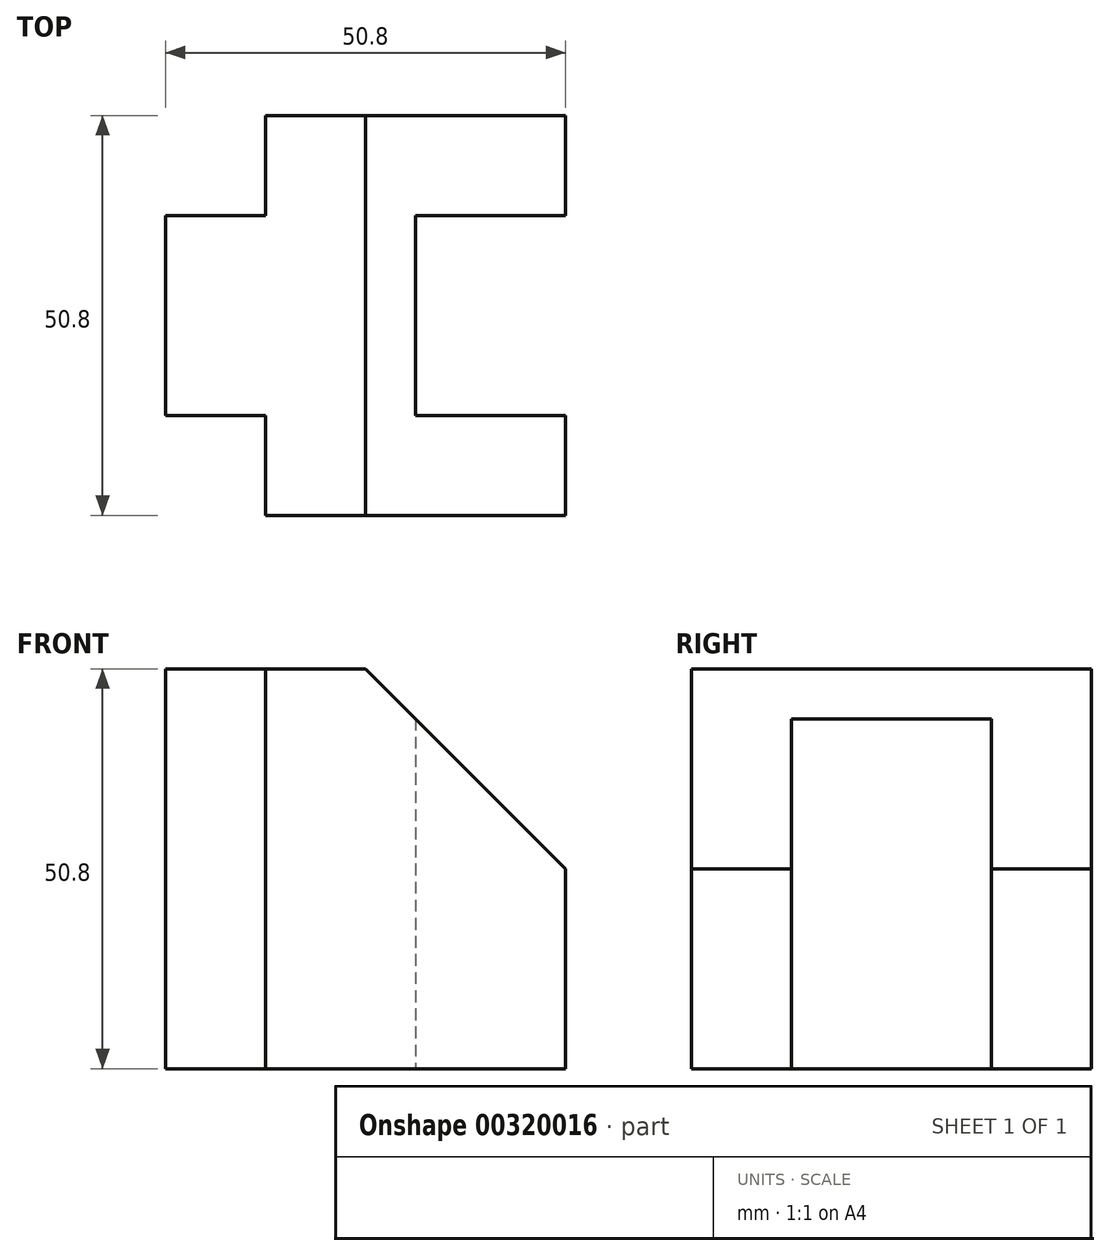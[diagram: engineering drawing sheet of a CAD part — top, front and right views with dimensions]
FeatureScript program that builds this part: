
annotation { "Feature Type Name" : "Feature", "Feature Type Description" : "" }
export const myFeature = defineFeature(function(context is Context, id is Id, definition is map)
    precondition{}
    {
        {
            var Q0;
            Q0=qCreatedBy(makeId("Top.planeOp"),FACE);
            var sketch = newSketch(context, id + "F0", { "sketchPlane" : qUnion([Q0])});
            skLineSegment(sketch, "E0", {"start": v(0, 12.7) * mm, "end": v(0, -12.7) * mm});
            skLineSegment(sketch, "E1", {"start": v(0, -12.7) * mm, "end": v(19.05, -12.7) * mm});
            skLineSegment(sketch, "E2", {"start": v(19.05, -12.7) * mm, "end": v(19.05, -25.4) * mm});
            skLineSegment(sketch, "E3", {"start": v(19.05, -25.4) * mm, "end": v(-19.05, -25.4) * mm});
            skLineSegment(sketch, "E4", {"start": v(-19.05, -25.4) * mm, "end": v(-19.05, -12.7) * mm});
            skLineSegment(sketch, "E5", {"start": v(-19.05, -12.7) * mm, "end": v(-31.75, -12.7) * mm});
            skLineSegment(sketch, "E6", {"start": v(-31.75, -12.7) * mm, "end": v(-31.75, 12.7) * mm});
            skLineSegment(sketch, "E7", {"start": v(-31.75, 12.7) * mm, "end": v(-19.05, 12.7) * mm});
            skLineSegment(sketch, "E8", {"start": v(-19.05, 12.7) * mm, "end": v(-19.05, 25.4) * mm});
            skLineSegment(sketch, "E9", {"start": v(-19.05, 25.4) * mm, "end": v(19.05, 25.4) * mm});
            skLineSegment(sketch, "E10", {"start": v(19.05, 25.4) * mm, "end": v(19.05, 12.7) * mm});
            skLineSegment(sketch, "E11", {"start": v(19.05, 12.7) * mm, "end": v(0, 12.7) * mm});
            skLineSegment(sketch, "E12", {"start": v(-6.35, 25.4) * mm, "end": v(-6.35, -25.4) * mm});
            skSolve(sketch);
        }
        {
            var Q0;
            {var subQ0=sQuery(id+"F0.wireOp",EDGE,"E4");Q0=makeQuery(id+"F0.imprint","IMPRINT",FACE,{"disambiguationData":[TD([[makeQuery(id+"F0.imprint","IMPRINT",EDGE,{"derivedFrom":subQ0}),-1.0]])]});}
            extrude(context, id + "F1", {"entities" : qUnion([Q0]), "depth" : 50.8 * mm});
        }
        {
            var Q0;
            Q0=makeQuery(id+"F0.imprint","IMPRINT",FACE,{"disambiguationData":[TD([[makeQuery(id+"F0.imprint","IMPRINT",EDGE,{"derivedFrom":sQuery(id+"F0.wireOp",EDGE,"E0")}),-1.0]])]});
            extrude(context, id + "F2", {"entities" : qUnion([Q0]), "operationType" : NewBodyOperationType.ADD, "depth" : 50.8 * mm});
        }
        {
            var Q0;
            {var subQ0=sQuery(id+"F0.wireOp",EDGE,"E3");Q0=makeQuery(id+"F2.boolean.opBoolean","MERGE",FACE,{"derivedFrom":[makeQuery(id+"F1.opExtrude","SWEPT_FACE",FACE,{"disambiguationData":[OSD([subQ0])]}),makeQuery(id+"F2.opExtrude","SWEPT_FACE",FACE,{"disambiguationData":[OSD([subQ0])]})]});}
            var sketch = newSketch(context, id + "F3", { "sketchPlane" : qUnion([Q0])});
            skLineSegment(sketch, "E13.0.0", {"start": v(-19.05, 0) * mm, "end": v(19.05, 0) * mm});
            skLineSegment(sketch, "E13.0.1", {"start": v(19.05, 0) * mm, "end": v(19.05, 50.8) * mm});
            skLineSegment(sketch, "E13.0.2", {"start": v(19.05, 50.8) * mm, "end": v(-19.05, 50.8) * mm});
            skLineSegment(sketch, "E13.0.3", {"start": v(-19.05, 50.8) * mm, "end": v(-19.05, 0) * mm});
            skLineSegment(sketch, "E14", {"start": v(-6.35, 50.8) * mm, "end": v(19.05, 25.4) * mm});
            skLineSegment(sketch, "E15", {"start": v(19.05, 25.4) * mm, "end": v(19.05, 50.8) * mm});
            skSolve(sketch);
        }
        {
            var Q0;
            {var subQ2=sQuery(id+"F3.wireOp",EDGE,"E14");Q0=makeQuery(id+"F3.imprint","IMPRINT",FACE,{"disambiguationData":[TD([[makeQuery(id+"F3.imprint","IMPRINT",EDGE,{"derivedFrom":subQ2}),1.0]])]});}
            extrude(context, id + "F4", {"entities" : qUnion([Q0]), "operationType" : NewBodyOperationType.REMOVE, "endBound" : BoundingType.THROUGH_ALL, "oppositeDirection" : true, "depth" : 25.4 * mm});
        }
    });
